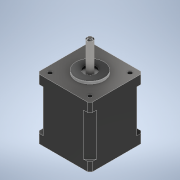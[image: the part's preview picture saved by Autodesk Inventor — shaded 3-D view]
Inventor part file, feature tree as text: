
AUTODESK INVENTOR PART (.ipt)
format: ipt  version: 2021 (Build 250183000, 183)  size: 231,936 bytes
history: native  units: mm
features: extrude x8, sketch x8, chamfer x3
ambient origin geometry x8: Origin, YZ Plane, XZ Plane, XY Plane, X Axis, Y Axis, Z Axis, Center Point
bodies: Solid1 (feature_tree)
feature tree (19):
  extrude  "Extrusion1"  Depth=42.0mm
  chamfer  "Chamfer1"  Distance=47.5mm
  extrude  "Extrusion2"  Depth=7.0mm TaperAngle=0.0deg
  extrude  "Extrusion3"  Depth=2.0mm TaperAngle=45.0deg
  chamfer  "Chamfer2"  Distance=7.0mm
  extrude  "Extrusion4"  Depth=22.0mm
  extrude  "Extrusion5"  Depth=2.0mm
  extrude  "Extrusion6"  Depth=2.0mm
  extrude  "Extrusion7"  Depth=2.0mm
  extrude  "Extrusion8"  Depth=2.0mm
  chamfer  "Chamfer3"  Distance=31.5mm
  sketch  "Sketch1"  dims[d0=42.0mm d1=42.0mm d2=47.5mm d3=0.0mm]
  sketch  "Sketch3"  dims[d4=5.0mm d5=2.0mm d6=45.0deg d7=7.0mm d8=0.0mm]
  sketch  "Sketch4"  dims[d9=7.0mm d10=0.0mm d11=2.0mm d12=2.0mm d13=45.0deg]
  sketch  "Sketch5"  dims[d14=10.0mm]
  sketch  "Sketch6"  dims[d15=21.0mm]
  sketch  "Sketch7"  dims[d16=21.0mm d17=7.0mm d18=0.0mm]
  sketch  "Sketch8"  dims[d19=10.0mm d20=22.0mm]
  sketch  "Sketch9"  dims[d21=2.0mm d22=0.0mm d23=3.2mm d24=3.2mm d25=3.2mm d26=3.2mm d27=31.5mm d28=31.5mm d29=31.5mm d30=31.5mm d31=5.25mm d32=5.25mm d33=5.25mm d34=5.25mm d35=10.0mm d36=0.0mm d37=3.2mm d38=3.2mm d39=3.2mm d40=3.2mm d41=2.0mm d42=0.0mm d43=5.0mm d44=21.0mm d45=21.0mm d46=24.0mm d47=0.0mm d48=1.0mm d49=2.0mm d50=45.0deg]
